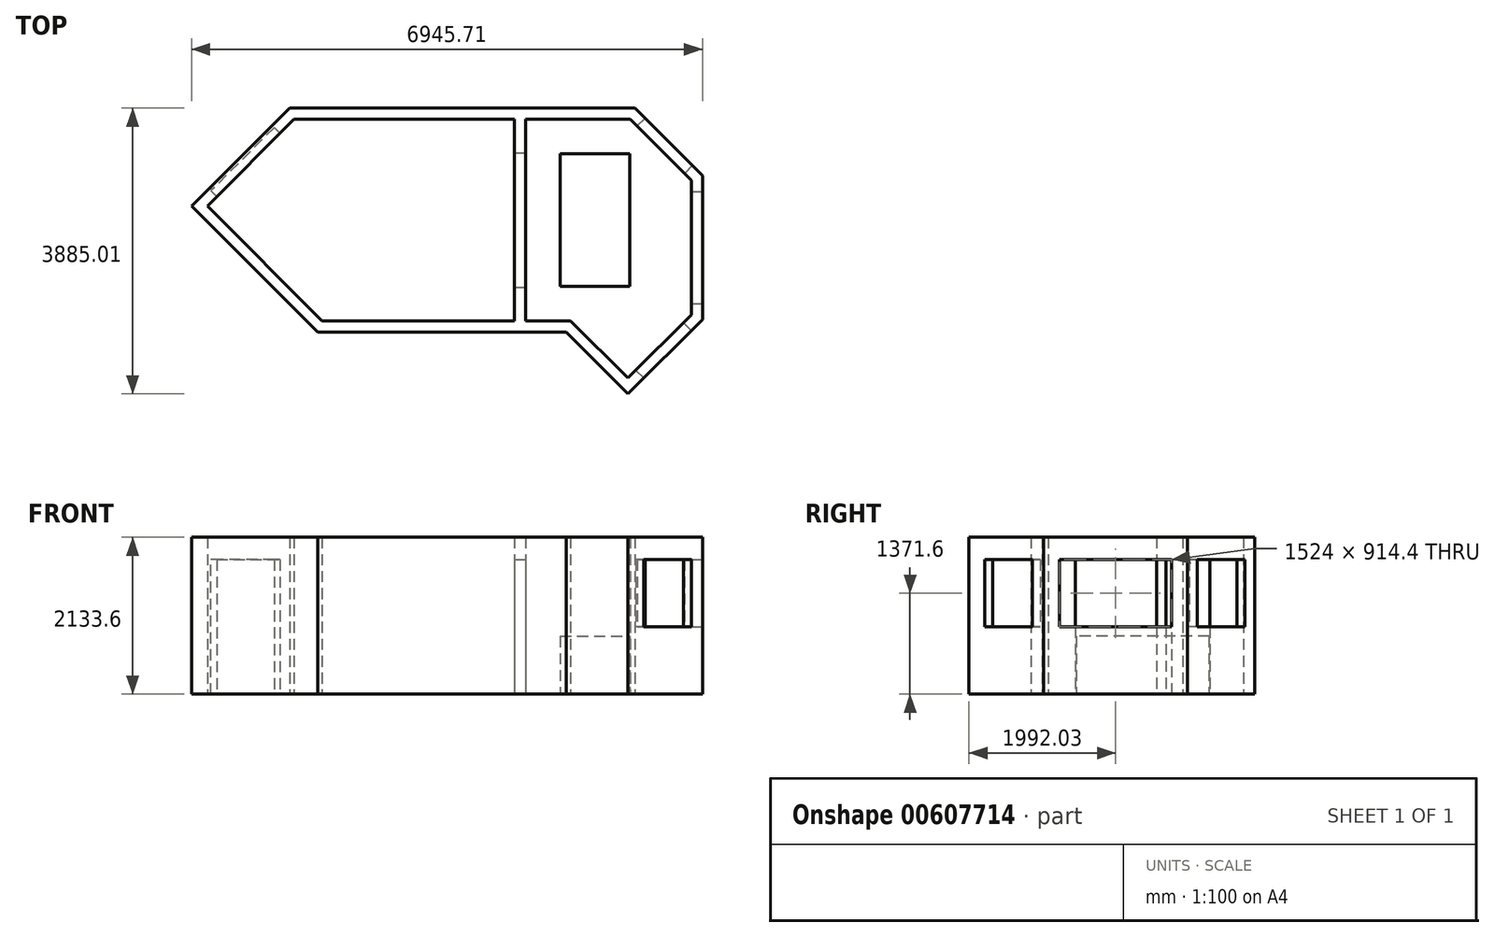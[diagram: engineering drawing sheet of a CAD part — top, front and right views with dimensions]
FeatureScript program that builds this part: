
annotation { "Feature Type Name" : "Feature", "Feature Type Description" : "" }
export const myFeature = defineFeature(function(context is Context, id is Id, definition is map)
    precondition{}
    {
        {
            var Q0;
            Q0=qCreatedBy(makeId("Top.planeOp"),FACE);
            var sketch = newSketch(context, id + "F0", { "sketchPlane" : qUnion([Q0])});
            skLineSegment(sketch, "E0", {"start": v(0, 0) * mm, "end": v(2997.2, 0) * mm});
            skLineSegment(sketch, "E1", {"start": v(2997.2, 0) * mm, "end": v(2997.2, -455.7) * mm});
            skLineSegment(sketch, "E2", {"start": v(2997.2, -455.7) * mm, "end": v(3149.6, -455.7) * mm});
            skLineSegment(sketch, "E3", {"start": v(3149.6, -455.7) * mm, "end": v(3149.6, 0) * mm});
            skLineSegment(sketch, "E4", {"start": v(3149.6, 0) * mm, "end": v(4572, 0) * mm});
            skLineSegment(sketch, "E5", {"start": v(4572, 0) * mm, "end": v(5398.18, -826.18) * mm});
            skLineSegment(sketch, "E6", {"start": v(5398.18, -826.18) * mm, "end": v(5398.18, -2654.98) * mm});
            skLineSegment(sketch, "E7", {"start": v(5398.18, -2654.98) * mm, "end": v(4536.08, -3517.09) * mm});
            skLineSegment(sketch, "E8", {"start": v(4536.08, -3517.09) * mm, "end": v(3759.2, -2740.2) * mm});
            skLineSegment(sketch, "E9", {"start": v(3759.2, -2740.2) * mm, "end": v(3149.6, -2740.2) * mm});
            skLineSegment(sketch, "E10", {"start": v(3149.6, -2740.2) * mm, "end": v(3149.6, -2284.5) * mm});
            skLineSegment(sketch, "E11", {"start": v(3149.6, -2284.5) * mm, "end": v(2997.2, -2284.5) * mm});
            skLineSegment(sketch, "E12", {"start": v(2997.2, -2284.5) * mm, "end": v(2997.2, -2740.2) * mm});
            skLineSegment(sketch, "E13", {"start": v(2997.2, -2740.2) * mm, "end": v(381, -2740.2) * mm});
            skLineSegment(sketch, "E14", {"start": v(381, -2740.2) * mm, "end": v(-1179.6, -1179.6) * mm});
            skLineSegment(sketch, "E15", {"start": v(-1179.6, -1179.6) * mm, "end": v(-1052.42, -1052.42) * mm});
            skLineSegment(sketch, "E16", {"start": v(-1052.42, -1052.42) * mm, "end": v(-1160.18, -944.65) * mm});
            skLineSegment(sketch, "E17", {"start": v(-1160.18, -944.65) * mm, "end": v(-1395.13, -1179.6) * mm});
            skLineSegment(sketch, "E18", {"start": v(-1395.13, -1179.6) * mm, "end": v(317.87, -2892.6) * mm});
            skLineSegment(sketch, "E19", {"start": v(317.87, -2892.6) * mm, "end": v(3696.07, -2892.6) * mm});
            skLineSegment(sketch, "E20", {"start": v(3696.07, -2892.6) * mm, "end": v(4536.08, -3732.61) * mm});
            skLineSegment(sketch, "E21", {"start": v(4536.08, -3732.61) * mm, "end": v(5550.58, -2718.1) * mm});
            skLineSegment(sketch, "E22", {"start": v(5550.58, -2718.1) * mm, "end": v(5550.58, -763.06) * mm});
            skLineSegment(sketch, "E23", {"start": v(5550.58, -763.06) * mm, "end": v(4635.13, 152.4) * mm});
            skLineSegment(sketch, "E24", {"start": v(4635.13, 152.4) * mm, "end": v(-63.13, 152.4) * mm});
            skLineSegment(sketch, "E25", {"start": v(-63.13, 152.4) * mm, "end": v(-298.08, -82.55) * mm});
            skLineSegment(sketch, "E26", {"start": v(-298.08, -82.55) * mm, "end": v(-190.31, -190.31) * mm});
            skLineSegment(sketch, "E27", {"start": v(-190.31, -190.31) * mm, "end": v(0, 0) * mm});
            skLineSegment(sketch, "E28", {"start": v(-463.12, -1896.09) * mm, "end": v(-570.88, -2003.85) * mm, "construction": true});
            skLineSegment(sketch, "E29", {"start": v(1689.1, -2740.2) * mm, "end": v(1689.1, -2892.6) * mm, "construction": true});
            skLineSegment(sketch, "E30", {"start": v(4147.64, -3128.65) * mm, "end": v(4039.88, -3236.41) * mm, "construction": true});
            skLineSegment(sketch, "E31", {"start": v(4967.13, -3086.04) * mm, "end": v(5074.9, -3193.8) * mm, "construction": true});
            skLineSegment(sketch, "E32", {"start": v(5550.58, -1740.58) * mm, "end": v(5398.18, -1740.58) * mm, "construction": true});
            skLineSegment(sketch, "E33", {"start": v(5092.85, -305.33) * mm, "end": v(4985.1, -413.1) * mm, "construction": true});
            skLineSegment(sketch, "E34", {"start": v(2286, 152.4) * mm, "end": v(2286, 0) * mm, "construction": true});
            skLineSegment(sketch, "E35", {"start": v(-1395.13, -1179.6) * mm, "end": v(-63.13, 152.4) * mm, "construction": true});
            skLineSegment(sketch, "E36", {"start": v(-729.13, -513.6) * mm, "end": v(-493.66, -749.08) * mm, "construction": true});
            skSolve(sketch);
        }
        {
            var Q0;
            Q0 = qSketchRegion(id + "F0", true);
            extrude(context, id + "F1", {"entities" : qUnion([Q0]), "depth" : 2133.6 * mm, "offsetDistance" : 25.4 * mm});
        }
        {
            var Q0;
            Q0=makeQuery(id+"F1.opExtrude","SWEPT_FACE",FACE,{"disambiguationData":[OSD([sQuery(id+"F0.wireOp",EDGE,"E25")])]});
            var sketch = newSketch(context, id + "F2", { "sketchPlane" : qUnion([Q0])});
            skLineSegment(sketch, "E37.bottom", {"start": v(269.14, 0) * mm, "end": v(878.74, 0) * mm});
            skLineSegment(sketch, "E37.top", {"start": v(269.14, 1828.8) * mm, "end": v(878.74, 1828.8) * mm});
            skLineSegment(sketch, "E37.left", {"start": v(269.14, 0) * mm, "end": v(269.14, 1828.8) * mm});
            skLineSegment(sketch, "E37.right", {"start": v(878.74, 0) * mm, "end": v(878.74, 1828.8) * mm});
            skSolve(sketch);
        }
        {
            var Q0;
            Q0 = qSketchRegion(id + "F2", true);
            extrude(context, id + "F3", {"entities" : qUnion([Q0]), "oppositeDirection" : true, "depth" : 38.1 * mm, "offsetDistance" : 25.4 * mm});
        }
        {
            var Q0;
            Q0=makeQuery(id+"F3.opExtrude","SWEPT_BODY",BODY,{"disambiguationData":[OSD([sQuery(id+"F2.wireOp",EDGE,"E37.bottom"),sQuery(id+"F2.wireOp",EDGE,"E37.top"),sQuery(id+"F2.wireOp",EDGE,"E37.left"),sQuery(id+"F2.wireOp",EDGE,"E37.right")])]});
            var Q1;
            Q1=makeQuery(id+"F3.opExtrude","CAP_EDGE",EDGE,{"disambiguationData":[OSD([sQuery(id+"F2.wireOp",EDGE,"E37.top")])],"isStart":true});
            transform(context, id + "F4", {"entities" : qUnion([Q0]), "transformType" : TransformType.TRANSLATION_DISTANCE, "transformDirection" : qUnion([Q1]), "distance" : 609.6 * mm, "makeCopy" : true});
        }
        {
            var Q0;
            Q0=makeQuery(id+"F1.opExtrude","SWEPT_FACE",FACE,{"disambiguationData":[OSD([sQuery(id+"F0.wireOp",EDGE,"E25")])]});
            var sketch = newSketch(context, id + "F5", { "sketchPlane" : qUnion([Q0])});
            skLineSegment(sketch, "E38.bottom", {"start": v(269.14, 2133.6) * mm, "end": v(1488.34, 2133.6) * mm});
            skLineSegment(sketch, "E38.top", {"start": v(269.14, 1828.8) * mm, "end": v(1488.34, 1828.8) * mm});
            skLineSegment(sketch, "E38.left", {"start": v(269.14, 2133.6) * mm, "end": v(269.14, 1828.8) * mm});
            skLineSegment(sketch, "E38.right", {"start": v(1488.34, 2133.6) * mm, "end": v(1488.34, 1828.8) * mm});
            skSolve(sketch);
        }
        {
            var Q0;
            Q0 = qSketchRegion(id + "F5", true);
            var Q1;
            Q1=makeQuery(id+"F1.opExtrude","SWEPT_FACE",FACE,{"disambiguationData":[OSD([sQuery(id+"F0.wireOp",EDGE,"E27")])]});
            extrude(context, id + "F6", {"entities" : qUnion([Q0]), "operationType" : NewBodyOperationType.ADD, "endBound" : BoundingType.UP_TO_SURFACE, "oppositeDirection" : true, "depth" : 152.4 * mm, "endBoundEntityFace" : qUnion([Q1]), "offsetDistance" : 25.4 * mm});
        }
        {
            var Q0;
            Q0=makeQuery(id+"F1.opExtrude","SWEPT_FACE",FACE,{"disambiguationData":[OSD([sQuery(id+"F0.wireOp",EDGE,"E22")])]});
            var sketch = newSketch(context, id + "F7", { "sketchPlane" : qUnion([Q0])});
            skLineSegment(sketch, "E39.bottom", {"start": v(-2502.58, 1828.8) * mm, "end": v(-978.58, 1828.8) * mm});
            skLineSegment(sketch, "E39.top", {"start": v(-2502.58, 914.4) * mm, "end": v(-978.58, 914.4) * mm});
            skLineSegment(sketch, "E39.left", {"start": v(-2502.58, 1828.8) * mm, "end": v(-2502.58, 914.4) * mm});
            skLineSegment(sketch, "E39.right", {"start": v(-978.58, 1828.8) * mm, "end": v(-978.58, 914.4) * mm});
            skLineSegment(sketch, "E40", {"start": v(-1740.58, 2133.6) * mm, "end": v(-1740.58, 1828.8) * mm, "construction": true});
            skPoint(sketch, "E40.endSnap0", {"position": v(-1740.58, 1828.8) * mm});
            skSolve(sketch);
        }
        {
            var Q0;
            Q0 = qSketchRegion(id + "F7", true);
            extrude(context, id + "F8", {"entities" : qUnion([Q0]), "operationType" : NewBodyOperationType.REMOVE, "endBound" : BoundingType.UP_TO_NEXT, "oppositeDirection" : true, "depth" : 25.4 * mm, "offsetDistance" : 25.4 * mm});
        }
        {
            var Q0;
            Q0=makeQuery(id+"F1.opExtrude","SWEPT_FACE",FACE,{"disambiguationData":[OSD([sQuery(id+"F0.wireOp",EDGE,"E10")])]});
            var sketch = newSketch(context, id + "F9", { "sketchPlane" : qUnion([Q0])});
            skLineSegment(sketch, "E41.bottom", {"start": v(-2284.5, 2133.6) * mm, "end": v(-455.7, 2133.6) * mm});
            skLineSegment(sketch, "E41.top", {"start": v(-2284.5, 1828.8) * mm, "end": v(-455.7, 1828.8) * mm});
            skLineSegment(sketch, "E41.left", {"start": v(-2284.5, 2133.6) * mm, "end": v(-2284.5, 1828.8) * mm});
            skLineSegment(sketch, "E41.right", {"start": v(-455.7, 2133.6) * mm, "end": v(-455.7, 1828.8) * mm});
            skSolve(sketch);
        }
        {
            var Q0;
            Q0 = qSketchRegion(id + "F9", true);
            var Q1;
            Q1=makeQuery(id+"F1.opExtrude","SWEPT_FACE",FACE,{"disambiguationData":[OSD([sQuery(id+"F0.wireOp",EDGE,"E1")])]});
            extrude(context, id + "F10", {"entities" : qUnion([Q0]), "operationType" : NewBodyOperationType.ADD, "endBound" : BoundingType.UP_TO_SURFACE, "oppositeDirection" : true, "depth" : 25.4 * mm, "endBoundEntityFace" : qUnion([Q1]), "offsetDistance" : 25.4 * mm});
        }
        {
            var Q0;
            Q0=makeQuery(id+"F1.opExtrude","SWEPT_FACE",FACE,{"disambiguationData":[OSD([sQuery(id+"F0.wireOp",EDGE,"E5")])]});
            var sketch = newSketch(context, id + "F11", { "sketchPlane" : qUnion([Q0])});
            skLineSegment(sketch, "E42.bottom", {"start": v(3359.9, 1828.8) * mm, "end": v(4274.3, 1828.8) * mm});
            skLineSegment(sketch, "E42.top", {"start": v(3359.9, 914.4) * mm, "end": v(4274.3, 914.4) * mm});
            skLineSegment(sketch, "E42.left", {"start": v(3359.9, 1828.8) * mm, "end": v(3359.9, 914.4) * mm});
            skLineSegment(sketch, "E42.right", {"start": v(4274.3, 1828.8) * mm, "end": v(4274.3, 914.4) * mm});
            skLineSegment(sketch, "E43", {"start": v(3817.1, 1828.8) * mm, "end": v(3817.1, 2133.6) * mm, "construction": true});
            skSolve(sketch);
        }
        {
            var Q0;
            Q0 = qSketchRegion(id + "F11", true);
            extrude(context, id + "F12", {"entities" : qUnion([Q0]), "operationType" : NewBodyOperationType.REMOVE, "endBound" : BoundingType.UP_TO_NEXT, "oppositeDirection" : true, "depth" : 25.4 * mm, "offsetDistance" : 25.4 * mm});
        }
        {
            var Q0;
            Q0=makeQuery(id+"F1.opExtrude","SWEPT_FACE",FACE,{"disambiguationData":[OSD([sQuery(id+"F0.wireOp",EDGE,"E7")])]});
            var sketch = newSketch(context, id + "F13", { "sketchPlane" : qUnion([Q0])});
            skLineSegment(sketch, "E44.bottom", {"start": v(-1787.34, 1828.8) * mm, "end": v(-872.94, 1828.8) * mm});
            skLineSegment(sketch, "E44.top", {"start": v(-1787.34, 914.4) * mm, "end": v(-872.94, 914.4) * mm});
            skLineSegment(sketch, "E44.left", {"start": v(-1787.34, 1828.8) * mm, "end": v(-1787.34, 914.4) * mm});
            skLineSegment(sketch, "E44.right", {"start": v(-872.94, 1828.8) * mm, "end": v(-872.94, 914.4) * mm});
            skLineSegment(sketch, "E45", {"start": v(-1330.14, 2133.6) * mm, "end": v(-1330.14, 1828.8) * mm, "construction": true});
            skSolve(sketch);
        }
        {
            var Q0;
            Q0 = qSketchRegion(id + "F13", true);
            extrude(context, id + "F14", {"entities" : qUnion([Q0]), "operationType" : NewBodyOperationType.REMOVE, "endBound" : BoundingType.UP_TO_NEXT, "oppositeDirection" : true, "depth" : 25.4 * mm, "offsetDistance" : 25.4 * mm});
        }
        {
            var Q0;
            Q0=qCreatedBy(makeId("Top.planeOp"),FACE);
            var sketch = newSketch(context, id + "F15", { "sketchPlane" : qUnion([Q0])});
            skLineSegment(sketch, "E46.bottom", {"start": v(3618, -468.4) * mm, "end": v(4565.42, -468.4) * mm});
            skLineSegment(sketch, "E46.top", {"start": v(3618, -2271.8) * mm, "end": v(4565.42, -2271.8) * mm});
            skLineSegment(sketch, "E46.left", {"start": v(3618, -468.4) * mm, "end": v(3618, -2271.8) * mm});
            skLineSegment(sketch, "E46.right", {"start": v(4565.42, -468.4) * mm, "end": v(4565.42, -2271.8) * mm});
            skLineSegment(sketch, "E47", {"start": v(3618, -1370.1) * mm, "end": v(3149.6, -1370.1) * mm, "construction": true});
            skPoint(sketch, "E47.endSnap0", {"position": v(3618, -1370.1) * mm});
            skLineSegment(sketch, "E48", {"start": v(3618, -468.4) * mm, "end": v(3618, 0) * mm, "construction": true});
            skSolve(sketch);
        }
        {
            var Q0;
            Q0 = qSketchRegion(id + "F15", true);
            extrude(context, id + "F16", {"entities" : qUnion([Q0]), "depth" : 787.4 * mm, "offsetDistance" : 25.4 * mm});
        }
    });
